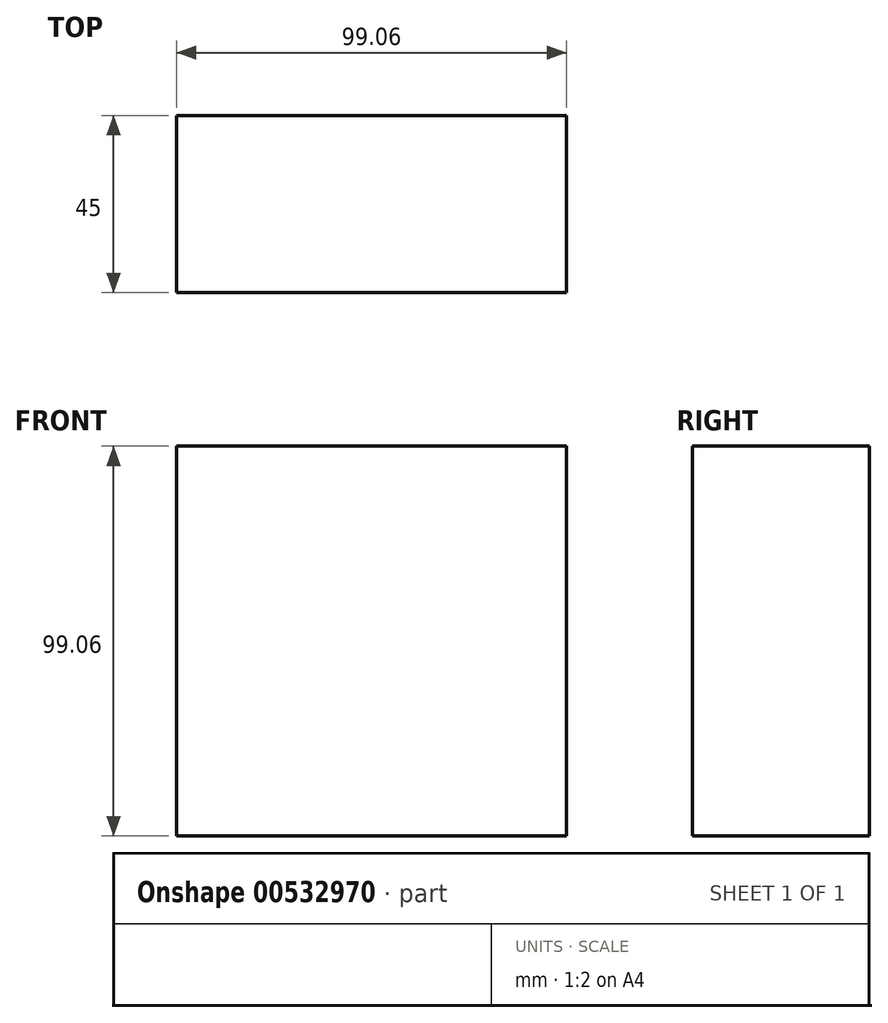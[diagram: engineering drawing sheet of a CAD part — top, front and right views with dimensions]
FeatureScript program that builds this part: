
annotation { "Feature Type Name" : "Feature", "Feature Type Description" : "" }
export const myFeature = defineFeature(function(context is Context, id is Id, definition is map)
    precondition{}
    {
        {
            var Q0;
            Q0=qCreatedBy(makeId("Front.planeOp"),FACE);
            var sketch = newSketch(context, id + "F0", { "sketchPlane" : qUnion([Q0])});
            skLineSegment(sketch, "E0.bottom", {"start": v(-50.75, 52.28) * mm, "end": v(48.31, 52.28) * mm});
            skLineSegment(sketch, "E0.top", {"start": v(-50.75, -46.78) * mm, "end": v(48.31, -46.78) * mm});
            skLineSegment(sketch, "E0.left", {"start": v(-50.75, 52.28) * mm, "end": v(-50.75, -46.78) * mm});
            skLineSegment(sketch, "E0.right", {"start": v(48.31, 52.28) * mm, "end": v(48.31, -46.78) * mm});
            skSolve(sketch);
        }
        {
            var Q0;
            Q0 = qSketchRegion(id + "F0", true);
            extrude(context, id + "F1", {"entities" : qUnion([Q0]), "depth" : 45 * mm, "offsetDistance" : 25.4 * mm});
        }
    });
